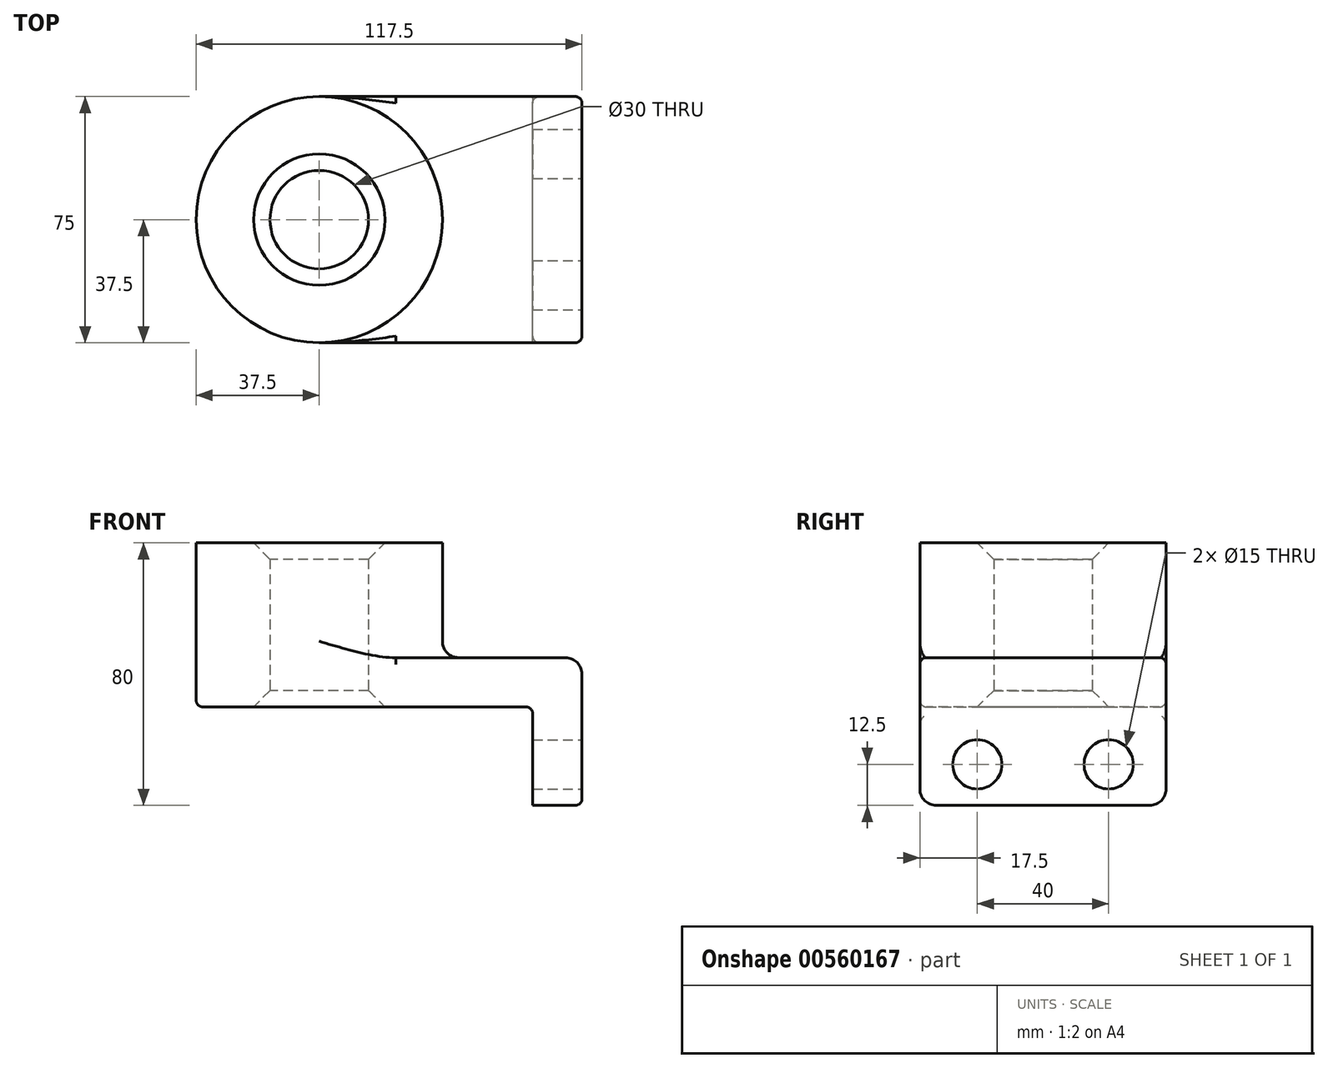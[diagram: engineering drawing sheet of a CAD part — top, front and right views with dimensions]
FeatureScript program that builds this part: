
annotation { "Feature Type Name" : "Feature", "Feature Type Description" : "" }
export const myFeature = defineFeature(function(context is Context, id is Id, definition is map)
    precondition{}
    {
        {
            var Q0;
            Q0=qCreatedBy(makeId("Top.planeOp"),FACE);
            var sketch = newSketch(context, id + "F0", { "sketchPlane" : qUnion([Q0])});
            skLineSegment(sketch, "E0.rect.bottom", {"start": v(-40, 37.5) * mm, "end": v(40, 37.5) * mm});
            skLineSegment(sketch, "E0.rect.top", {"start": v(-40, -37.5) * mm, "end": v(40, -37.5) * mm});
            skLineSegment(sketch, "E0.rect.left", {"start": v(-40, 37.5) * mm, "end": v(-40, -37.5) * mm});
            skLineSegment(sketch, "E0.rect.right", {"start": v(40, 37.5) * mm, "end": v(40, -37.5) * mm});
            skPoint(sketch, "E0.rect.middle", {"position": v(0, 0) * mm});
            skCircle(sketch, "E1", {"center": v(-40, 0) * mm, "radius": 37.5 * mm});
            skCircle(sketch, "E2", {"center": v(-40, 0) * mm, "radius": 15 * mm});
            skSolve(sketch);
        }
        {
            var Q0;
            Q0=qSketchRegion(id+"F0",true);
            extrude(context, id + "F1", {"entities" : qUnion([Q0]), "depth" : 15 * mm});
        }
        {
            var Q0;
            {var subQ0=sQuery(id+"F0.wireOp",EDGE,"E2");var subQ1=sQuery(id+"F0.wireOp",EDGE,"E0.rect.left");var subQ3=makeQuery(id+"F0.imprint","INTERSECT",VERTEX,{"disambiguationData":[OD(0.0)],"derivedFrom":[subQ1,subQ0]});Q0=makeQuery(id+"F0.imprint","IMPRINT",FACE,{"disambiguationData":[TD([[makeQuery(id+"F0.imprint","IMPRINT",EDGE,{"disambiguationData":[TD([[subQ3,-1.0]])],"derivedFrom":subQ0}),-1.0]])]});}
            var Q1;
            {var subQ0=sQuery(id+"F0.wireOp",EDGE,"E2");var subQ1=sQuery(id+"F0.wireOp",EDGE,"E0.rect.left");var subQ3=makeQuery(id+"F0.imprint","INTERSECT",VERTEX,{"disambiguationData":[OD(0.0)],"derivedFrom":[subQ1,subQ0]});Q1=makeQuery(id+"F0.imprint","IMPRINT",FACE,{"disambiguationData":[TD([[makeQuery(id+"F0.imprint","IMPRINT",EDGE,{"disambiguationData":[TD([[subQ3,1.0]])],"derivedFrom":subQ0}),-1.0]])]});}
            extrude(context, id + "F2", {"entities" : qUnion([Q0, Q1]), "operationType" : NewBodyOperationType.ADD, "depth" : 50 * mm});
        }
        {
            var Q0;
            Q0=makeQuery(id+"F1.opExtrude","SWEPT_FACE",FACE,{"disambiguationData":[OSD([sQuery(id+"F0.wireOp",EDGE,"E0.rect.right")])]});
            var sketch = newSketch(context, id + "F3", { "sketchPlane" : qUnion([Q0])});
            skLineSegment(sketch, "E3.bottom", {"start": v(-37.5, 15) * mm, "end": v(37.5, 15) * mm});
            skLineSegment(sketch, "E3.top", {"start": v(-37.5, -30) * mm, "end": v(37.5, -30) * mm});
            skLineSegment(sketch, "E3.left", {"start": v(-37.5, 15) * mm, "end": v(-37.5, -30) * mm});
            skLineSegment(sketch, "E3.right", {"start": v(37.5, 15) * mm, "end": v(37.5, -30) * mm});
            skCircle(sketch, "E4", {"center": v(-20, -17.5) * mm, "radius": 7.5 * mm});
            skLineSegment(sketch, "E5", {"start": v(0, 0) * mm, "end": v(0, -30) * mm, "construction": true});
            skCircle(sketch, "E6.MirrorC", {"center": v(20, -17.5) * mm, "radius": 7.5 * mm});
            skSolve(sketch);
        }
        {
            var Q0;
            Q0=qSketchRegion(id+"F3",true);
            extrude(context, id + "F4", {"entities" : qUnion([Q0]), "operationType" : NewBodyOperationType.ADD, "oppositeDirection" : true, "depth" : 15 * mm});
        }
        {
            var Q0;
            {var subQ0=sQuery(id+"F0.wireOp",EDGE,"E1");Q0=makeQuery(id+"F2.boolean.opBoolean","INTERSECT",EDGE,{"derivedFrom":[makeQuery(id+"F1.opExtrude","CAP_FACE",FACE,{"disambiguationData":[OSD([sQuery(id+"F0.wireOp",EDGE,"E0.rect.bottom"),sQuery(id+"F0.wireOp",EDGE,"E0.rect.top"),sQuery(id+"F0.wireOp",EDGE,"E0.rect.right"),subQ0,sQuery(id+"F0.wireOp",EDGE,"E2")])],"isStart":false}),makeQuery(id+"F2.opExtrude","SWEPT_FACE",FACE,{"disambiguationData":[OSD([subQ0])]})]});}
            var Q1;
            Q1=makeQuery(id+"F1.opExtrude","CAP_EDGE",EDGE,{"disambiguationData":[OSD([sQuery(id+"F0.wireOp",EDGE,"E0.rect.right")])],"isStart":false});
            var Q2;
            Q2=makeQuery(id+"F4.opExtrude","SWEPT_EDGE",EDGE,{"disambiguationData":[OSD([sQuery(id+"F3.wireOp",EDGE,"E3.top"),sQuery(id+"F3.wireOp",EDGE,"E3.left")])]});
            var Q3;
            Q3=makeQuery(id+"F4.opExtrude","SWEPT_EDGE",EDGE,{"disambiguationData":[OSD([sQuery(id+"F3.wireOp",EDGE,"E3.top"),sQuery(id+"F3.wireOp",EDGE,"E3.right")])]});
            fillet(context, id + "F5", {"entities" : qUnion([Q0, Q1, Q2, Q3]), "radius" : 5 * mm, "tangentPropagation" : true, "allowEdgeOverflow" : false});
        }
        {
            var Q0;
            Q0=makeQuery(id+"F1.opExtrude","CAP_EDGE",EDGE,{"disambiguationData":[OSD([sQuery(id+"F0.wireOp",EDGE,"E0.rect.top")])],"isStart":false});
            var Q1;
            Q1=makeQuery(id+"F1.opExtrude","CAP_EDGE",EDGE,{"disambiguationData":[OSD([sQuery(id+"F0.wireOp",EDGE,"E0.rect.top")])],"isStart":true});
            var Q2;
            Q2=makeQuery(id+"F4.boolean.opBoolean","INTERSECT",EDGE,{"derivedFrom":[makeQuery(id+"F1.opExtrude","CAP_FACE",FACE,{"disambiguationData":[OSD([sQuery(id+"F0.wireOp",EDGE,"E0.rect.bottom"),sQuery(id+"F0.wireOp",EDGE,"E0.rect.top"),sQuery(id+"F0.wireOp",EDGE,"E0.rect.right"),sQuery(id+"F0.wireOp",EDGE,"E1"),sQuery(id+"F0.wireOp",EDGE,"E2")])],"isStart":true}),makeQuery(id+"F4.opExtrude","CAP_FACE",FACE,{"disambiguationData":[OSD([sQuery(id+"F3.wireOp",EDGE,"E3.bottom"),sQuery(id+"F3.wireOp",EDGE,"E3.top"),sQuery(id+"F3.wireOp",EDGE,"E3.left"),sQuery(id+"F3.wireOp",EDGE,"E3.right"),sQuery(id+"F3.wireOp",EDGE,"E4"),sQuery(id+"F3.wireOp",EDGE,"E6.MirrorC")])],"isStart":false})]});
            fillet(context, id + "F6", {"entities" : qUnion([Q0, Q1, Q2]), "radius" : 2 * mm, "tangentPropagation" : true, "allowEdgeOverflow" : false});
        }
        {
            var Q0;
            {var subQ0=sQuery(id+"F0.wireOp",EDGE,"E2");Q0=makeQuery(id+"F2.boolean.opBoolean","MERGE",FACE,{"derivedFrom":[makeQuery(id+"F1.opExtrude","SWEPT_FACE",FACE,{"disambiguationData":[OSD([subQ0])]}),makeQuery(id+"F2.opExtrude","SWEPT_FACE",FACE,{"disambiguationData":[OSD([subQ0])]})]});}
            chamfer(context, id + "F7", {"entities" : qUnion([Q0]), "width" : 5 * mm, "tangentPropagation" : true});
        }
    });
